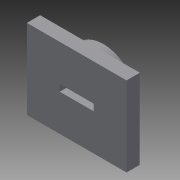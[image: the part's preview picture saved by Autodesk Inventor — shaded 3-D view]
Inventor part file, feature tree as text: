
AUTODESK INVENTOR PART (.ipt)
format: ipt  version: 2015 SP2 (Build 190223200, 223)  size: 114,688 bytes
history: native  units: mm
features: sketch x5, extrude x5
ambient origin geometry x8: Origin, YZ Plane, XZ Plane, XY Plane, X Axis, Y Axis, Z Axis, Center Point
bodies: Solid1 (feature_tree)
feature tree (10):
  sketch  "Sketch1"  dims[d0=5.1mm d1=1.0mm]
  sketch  "Sketch2"  dims[d2=15.0mm d3=12.0mm]
  extrude  "Extrusion1"  Depth=1.0mm
  extrude  "Extrusion2"  Depth=12.0mm
  extrude  "Extrusion4"  Depth=2.0mm TaperAngle=0.0deg
  extrude  "Extrusion5"  Depth=4.0mm TaperAngle=0.0deg
  extrude  "Extrusion6"  Depth=5.1mm
  sketch  "Sketch3"  dims[d4=10.0mm d5=2.0mm d6=0.0mm]
  sketch  "Sketch7"  dims[d7=2.0mm d8=0.0mm d11=4.0mm d12=0.0mm]
  sketch  "Sketch8"  dims[d13=3.0mm d14=0.0mm d15=5.1mm d16=1.0mm d17=3.0mm d18=0.0mm]
